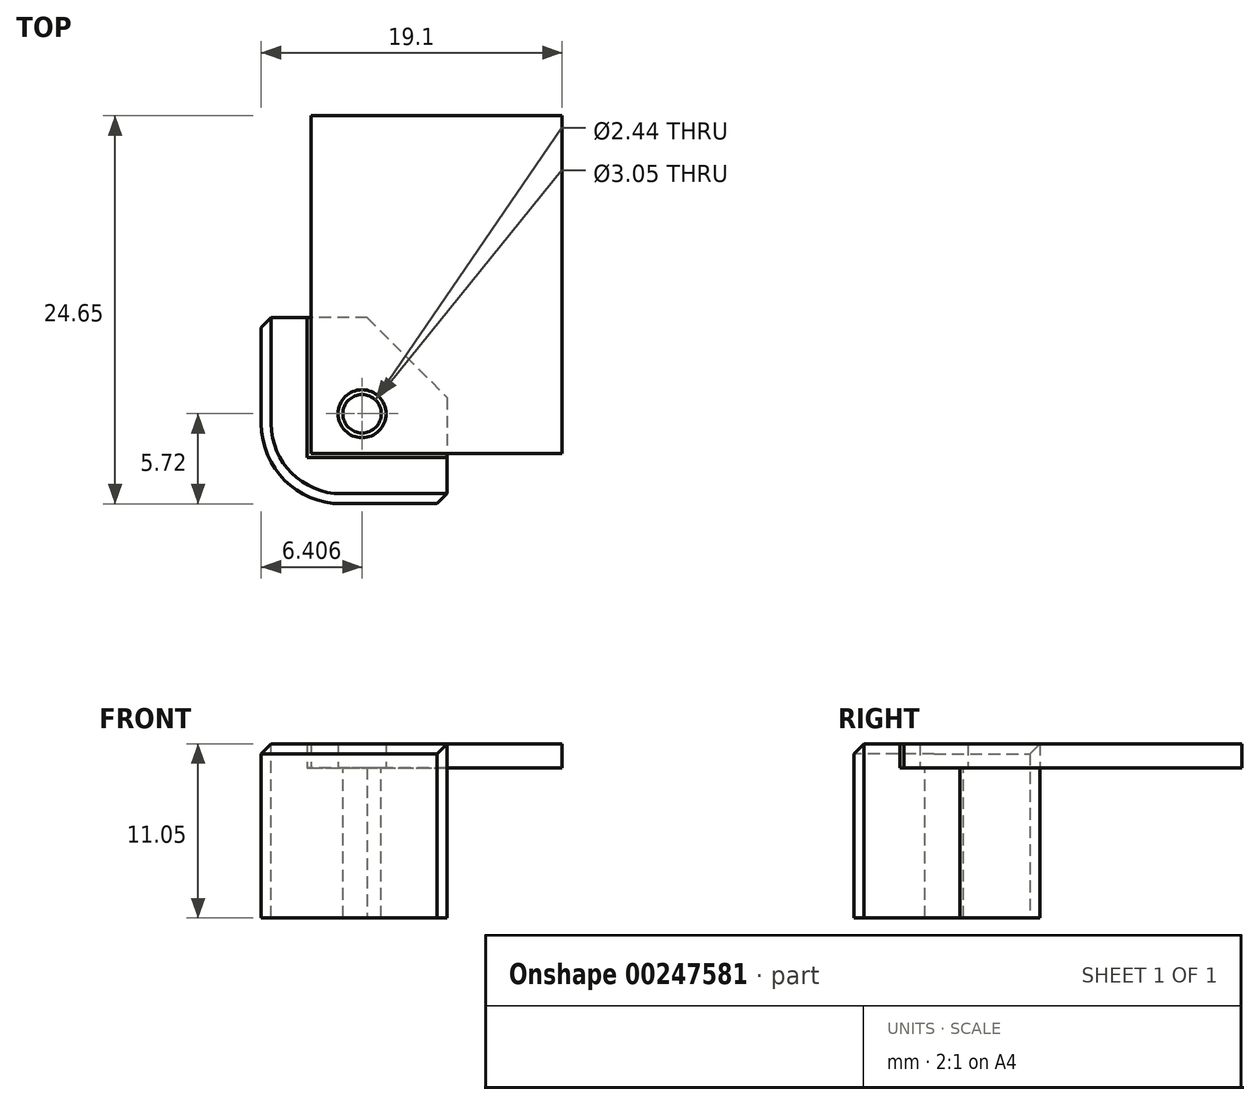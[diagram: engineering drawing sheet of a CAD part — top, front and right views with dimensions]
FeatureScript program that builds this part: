
annotation { "Feature Type Name" : "Feature", "Feature Type Description" : "" }
export const myFeature = defineFeature(function(context is Context, id is Id, definition is map)
    precondition{}
    {
        {
            var Q0;
            Q0=qCreatedBy(makeId("Top.planeOp"),FACE);
            var sketch = newSketch(context, id + "F0", { "sketchPlane" : qUnion([Q0])});
            skLineSegment(sketch, "E0.bottom", {"start": v(0, 0) * mm, "end": v(15.92, 0) * mm});
            skLineSegment(sketch, "E0.top", {"start": v(0, 21.47) * mm, "end": v(15.92, 21.47) * mm});
            skLineSegment(sketch, "E0.left", {"start": v(0, 0) * mm, "end": v(0, 21.47) * mm});
            skLineSegment(sketch, "E0.right", {"start": v(15.92, 0) * mm, "end": v(15.92, 21.47) * mm});
            skCircle(sketch, "E1", {"center": v(3.23, 2.54) * mm, "radius": 1.52 * mm});
            skLineSegment(sketch, "E2", {"start": v(3.23, 1.02) * mm, "end": v(3.23, 0) * mm, "construction": true});
            skLineSegment(sketch, "E3", {"start": v(1.7, 2.54) * mm, "end": v(0, 2.54) * mm, "construction": true});
            skSolve(sketch);
        }
        {
            var Q0;
            Q0 = qSketchRegion(id + "F0", true);
            extrude(context, id + "F1", {"entities" : qUnion([Q0]), "depth" : 1.52 * mm});
        }
        {
            var Q0;
            Q0=makeQuery(id+"F1.opExtrude","CAP_FACE",FACE,{"disambiguationData":[OSD([sQuery(id+"F0.wireOp",EDGE,"E0.bottom"),sQuery(id+"F0.wireOp",EDGE,"E0.top"),sQuery(id+"F0.wireOp",EDGE,"E0.left"),sQuery(id+"F0.wireOp",EDGE,"E0.right"),sQuery(id+"F0.wireOp",EDGE,"E1")])],"isStart":true});
            var sketch = newSketch(context, id + "F2", { "sketchPlane" : qUnion([Q0])});
            skLineSegment(sketch, "E4.bottom", {"start": v(8.64, -8.64) * mm, "end": v(-3.17, -8.64) * mm});
            skLineSegment(sketch, "E4.top", {"start": v(8.64, 3.18) * mm, "end": v(-3.17, 3.17) * mm});
            skLineSegment(sketch, "E4.left", {"start": v(8.64, -8.64) * mm, "end": v(8.64, 3.18) * mm});
            skLineSegment(sketch, "E4.right", {"start": v(-3.17, -8.64) * mm, "end": v(-3.17, 3.17) * mm});
            skLineSegment(sketch, "E5", {"start": v(0, 3.18) * mm, "end": v(0, 0) * mm, "construction": true});
            skLineSegment(sketch, "E6", {"start": v(0, 0) * mm, "end": v(-3.17, 0) * mm, "construction": true});
            skSolve(sketch);
        }
        {
            var Q0;
            Q0 = qSketchRegion(id + "F2", true);
            extrude(context, id + "F3", {"entities" : qUnion([Q0]), "depth" : 9.52 * mm});
        }
        {
            var Q0;
            Q0=makeQuery(id+"F3.opExtrude","CAP_FACE",FACE,{"disambiguationData":[OSD([sQuery(id+"F2.wireOp",EDGE,"E4.bottom"),sQuery(id+"F2.wireOp",EDGE,"E4.top"),sQuery(id+"F2.wireOp",EDGE,"E4.left"),sQuery(id+"F2.wireOp",EDGE,"E4.right")])],"isStart":true});
            var sketch = newSketch(context, id + "F4", { "sketchPlane" : qUnion([Q0])});
            skLineSegment(sketch, "E7", {"start": v(-3.17, 8.64) * mm, "end": v(-0.25, 8.64) * mm});
            skLineSegment(sketch, "E8", {"start": v(-0.25, 8.64) * mm, "end": v(-0.25, -0.25) * mm});
            skLineSegment(sketch, "E9", {"start": v(-0.25, -0.25) * mm, "end": v(8.64, -0.25) * mm});
            skLineSegment(sketch, "E10", {"start": v(8.64, -0.25) * mm, "end": v(8.64, -3.18) * mm});
            skLineSegment(sketch, "E11", {"start": v(8.64, -3.18) * mm, "end": v(-3.17, -3.17) * mm});
            skLineSegment(sketch, "E12", {"start": v(-3.17, -3.18) * mm, "end": v(-3.17, 8.64) * mm});
            skLineSegment(sketch, "E13", {"start": v(-0.25, 8.64) * mm, "end": v(0, 8.64) * mm, "construction": true});
            skLineSegment(sketch, "E14", {"start": v(8.64, -0.25) * mm, "end": v(8.64, 0) * mm, "construction": true});
            skSolve(sketch);
        }
        {
            var Q0;
            Q0 = qSketchRegion(id + "F4", true);
            extrude(context, id + "F5", {"entities" : qUnion([Q0]), "operationType" : NewBodyOperationType.ADD, "depth" : 1.52 * mm});
        }
        {
            var Q0;
            Q0=makeQuery(id+"F3.opExtrude","CAP_FACE",FACE,{"disambiguationData":[OSD([sQuery(id+"F2.wireOp",EDGE,"E4.bottom"),sQuery(id+"F2.wireOp",EDGE,"E4.top"),sQuery(id+"F2.wireOp",EDGE,"E4.left"),sQuery(id+"F2.wireOp",EDGE,"E4.right")])],"isStart":true});
            var sketch = newSketch(context, id + "F6", { "sketchPlane" : qUnion([Q0])});
            skPoint(sketch, "E15", {"position": v(3.23, 2.54) * mm});
            skSolve(sketch);
        }
        {
            var Q0;
            Q0=sQuery(id+"F6.wireOp",VERTEX,"E15");
            var Q1;
            Q1=makeQuery(id+"F3.opExtrude","SWEPT_BODY",BODY,{"disambiguationData":[OSD([sQuery(id+"F2.wireOp",EDGE,"E4.bottom"),sQuery(id+"F2.wireOp",EDGE,"E4.top"),sQuery(id+"F2.wireOp",EDGE,"E4.left"),sQuery(id+"F2.wireOp",EDGE,"E4.right")])]});
            hole(context, id + "F7", {"style" : HoleStyle.SIMPLE, "endStyle" : HoleEndStyle.THROUGH, "standardTappedOrClearance" : lookupTablePath({ "standard" : "ANSI", "fit" : "Normal (ASME)", "size" : "#2", "type" : "Clearance" }), "standardBlindInLast" : lookupTablePath({ "fit" : "Free", "standard" : "ANSI", "size" : "#2", "type" : "Clearance" }), "holeDiameter" : 2.44 * mm, "tappedDepth" : 12.7 * mm, "tapClearance" : 3, "locations" : qUnion([Q0]), "scope" : qUnion([Q1])});
        }
        {
            var Q0;
            Q0=makeQuery(id+"F5.boolean.opBoolean","MERGE",EDGE,{"derivedFrom":[makeQuery(id+"F3.opExtrude","SWEPT_EDGE",EDGE,{"disambiguationData":[OSD([sQuery(id+"F2.wireOp",EDGE,"E4.top"),sQuery(id+"F2.wireOp",EDGE,"E4.right")])]}),makeQuery(id+"F5.opExtrude","SWEPT_EDGE",EDGE,{"disambiguationData":[OSD([sQuery(id+"F4.wireOp",EDGE,"E11"),sQuery(id+"F4.wireOp",EDGE,"E12")])]})]});
            fillet(context, id + "F8", {"entities" : qUnion([Q0]), "radius" : 5.08 * mm, "tangentPropagation" : true, "allowEdgeOverflow" : false});
        }
        {
            var Q0;
            Q0=makeQuery(id+"F3.opExtrude","SWEPT_EDGE",EDGE,{"disambiguationData":[OSD([sQuery(id+"F2.wireOp",EDGE,"E4.bottom"),sQuery(id+"F2.wireOp",EDGE,"E4.left")])]});
            chamfer(context, id + "F9", {"entities" : qUnion([Q0]), "width" : 5.08 * mm, "tangentPropagation" : true});
        }
        {
            var Q0;
            Q0=makeQuery(id+"F5.boolean.opBoolean","MERGE",EDGE,{"derivedFrom":[makeQuery(id+"F3.opExtrude","SWEPT_EDGE",EDGE,{"disambiguationData":[OSD([sQuery(id+"F2.wireOp",EDGE,"E4.top"),sQuery(id+"F2.wireOp",EDGE,"E4.left")])]}),makeQuery(id+"F5.opExtrude","SWEPT_EDGE",EDGE,{"disambiguationData":[OSD([sQuery(id+"F4.wireOp",EDGE,"E10"),sQuery(id+"F4.wireOp",EDGE,"E11")])]})]});
            var Q1;
            Q1=makeQuery(id+"F5.boolean.opBoolean","MERGE",EDGE,{"derivedFrom":[makeQuery(id+"F3.opExtrude","SWEPT_EDGE",EDGE,{"disambiguationData":[OSD([sQuery(id+"F2.wireOp",EDGE,"E4.bottom"),sQuery(id+"F2.wireOp",EDGE,"E4.right")])]}),makeQuery(id+"F5.opExtrude","SWEPT_EDGE",EDGE,{"disambiguationData":[OSD([sQuery(id+"F4.wireOp",EDGE,"E7"),sQuery(id+"F4.wireOp",EDGE,"E12")])]})]});
            chamfer(context, id + "F10", {"entities" : qUnion([Q0, Q1]), "width" : 0.64 * mm, "tangentPropagation" : true});
        }
        {
            var Q0;
            Q0=makeQuery(id+"F5.opExtrude","CAP_EDGE",EDGE,{"disambiguationData":[OSD([sQuery(id+"F4.wireOp",EDGE,"E11")])],"isStart":false});
            var Q1;
            {var subQ0=sQuery(id+"F4.wireOp",EDGE,"E12");var subQ1=sQuery(id+"F4.wireOp",EDGE,"E11");Q1=makeQuery(id+"F8.opFillet","BLEND_EDGE",EDGE,{"blendedFrom":[makeQuery(id+"F5.boolean.opBoolean","MERGE",EDGE,{"derivedFrom":[makeQuery(id+"F3.opExtrude","SWEPT_EDGE",EDGE,{"disambiguationData":[OSD([sQuery(id+"F2.wireOp",EDGE,"E4.top"),sQuery(id+"F2.wireOp",EDGE,"E4.right")])]}),makeQuery(id+"F5.opExtrude","SWEPT_EDGE",EDGE,{"disambiguationData":[OSD([subQ1,subQ0])]})]}),makeQuery(id+"F5.opExtrude","CAP_FACE",FACE,{"disambiguationData":[OSD([sQuery(id+"F4.wireOp",EDGE,"E7"),sQuery(id+"F4.wireOp",EDGE,"E8"),sQuery(id+"F4.wireOp",EDGE,"E9"),sQuery(id+"F4.wireOp",EDGE,"E10"),subQ1,subQ0])],"isStart":false})],"blendedInto":[makeQuery(id+"F5.opExtrude","CAP_FACE",FACE,{"disambiguationData":[OSD([sQuery(id+"F4.wireOp",EDGE,"E7"),sQuery(id+"F4.wireOp",EDGE,"E8"),sQuery(id+"F4.wireOp",EDGE,"E9"),sQuery(id+"F4.wireOp",EDGE,"E10"),subQ1,subQ0])],"isStart":false})]});}
            var Q2;
            Q2=makeQuery(id+"F5.opExtrude","CAP_EDGE",EDGE,{"disambiguationData":[OSD([sQuery(id+"F4.wireOp",EDGE,"E12")])],"isStart":false});
            chamfer(context, id + "F11", {"entities" : qUnion([Q0, Q1, Q2]), "width" : 0.64 * mm, "tangentPropagation" : true});
        }
    });
